# Revit family: Grohe_PlumbingFixture_TempestaCosmopolitan100_ShowerRailSet_27579002a
name_source: partatom
category: Plumbing Fixtures
revit_build: Autodesk Revit 2018 (Build: 20190510_1515(x64)
units: mm (PartAtom-declared; Revit-internal decimal feet)

## family parameters
Cut with Voids When Loaded = No
Host = Face
OmniClass Number = 23.65.00.00
OmniClass Title = Supply and Distribution of Liquids and Gases
Part Type = Normal
Room Calculation Point = No
Round Connector Dimension = Use Diameter
Shared = No

## types (1)
- 27579002
    ADACompliant = No
    Assembly Code = D2010700
    BIMObjectName = Grohe_PlumbingFixture_TempestaCosmopolitan100_ShowerRailSet_27579002
    ClassificationName = Uniclass 2015
    ClassificationValue = Pr_40_20_87_75
    ColdWaterConnectionDiameter = 10 mm  [stored 0.0328084 ft]
    Color = Chrome
    Default Elevation = 0 mm  [stored 0 ft]
    Description = Add affordable luxury to your bathroom and change the way you shower with the GROHE New Tempesta Cosmopolitan 100 shower rail set. The stylish kit contains a hand shower with a white 100mm spray plate, a 600mm shower rail and a 1750mm hose. It’s packed with a lot of smart features. GROHE EcoJoy technology limits water flow to 9.5 l/m, which saves water and money without compromising performance. The hand shower comes with three spray options so you can tailor it to your mood: the light-as-air GROHE Rain O² Spray with added oxygen for a softer feel, the gentle summer shower feel of Rain Spray and the invigorating Massage Spray. GROHE DreamSpray ensures that whichever spray pattern you select, the flow from each and every nozzle will be just right, making your shower as comfortable and enjoyable as can be. Its SpeedClean silicone nozzles are designed to brush free of limescale with a simple wipe, and the durable GROHE StarLight chrome finish keeps the whole set looking pristine. And an Inner WaterGuide prevents the surface of the hand shower from getting too hot, in order to protect both your sensitive skin and the lustrous chrome finish.
    DocumentationCertificates = https://www.bimstore.co
    DocumentationInstallationGuide = https://www.bimstore.co
    DocumentationLiterature = https://www.bimstore.co
    DocumentationMaintenance = https://www.bimstore.co
    DocumentationTechnical = https://www.bimstore.co
    DurationUnit = Years
    Ecojoy = No
    ExpectedLife = 0
    Features = Add affordable luxury to your bathroom and change the way you shower with the GROHE New Tempesta Cosmopolitan 100 shower rail set. The stylish kit contains a hand shower with a white 100mm spray plate, a 600mm shower rail and a 1750mm hose. It’s packed with a lot of smart features. GROHE EcoJoy technology limits water flow to 9.5 l/m, which saves water and money without compromising performance. The hand shower comes with three spray options so you can tailor it to your mood: the light-as-air GROHE Rain O² Spray with added oxygen for a softer feel, the gentle summer shower feel of Rain Spray and the invigorating Massage Spray. GROHE DreamSpray ensures that whichever spray pattern you select, the flow from each and every nozzle will be just right, making your shower as comfortable and enjoyable as can be. Its SpeedClean silicone nozzles are designed to brush free of limescale with a simple wipe, and the durable GROHE StarLight chrome finish keeps the whole set looking pristine. And an Inner WaterGuide prevents the surface of the hand shower from getting too hot, in order to protect both your sensitive skin and the lustrous chrome finish.
    HotWaterConnectionDiameter = 10 mm  [stored 0.0328084 ft]
    IfcExportAs = IfcPipeFitting
    IfcExportType = IfcPipeFittingType
    Keynote = N13
    LowEmittingMaterial = No
    Manufacturer = Grohe
    ManufacturerName = Grohe
    MasterformatNumber = 01 52 19
    MasterformatTitle = Sanitary Facilities
    Model = Tempesta Cosmopolitan 100 - Shower rail set 3 sprays
    ModelNumber = 27579002
    ModelReference = Tempesta Cosmopolitan 100 - Shower rail set 3 sprays
    NBSDescription = Shower fittings package
    NBSObjectName = Grohe - Shower fittings package
    NBSReference = 45-35-70/330
    NominalDepth = 0 mm  [stored 0 ft]
    NominalHeight = 0 mm  [stored 0 ft]
    NominalLength = 0 mm  [stored 0 ft]
    PrimaryMaterial = Steel, Chrome Plated
    ProductDocumentationLink = https://www.grohe.co.uk
    ProductPageURL = https://www.grohe.co.uk
    ProductionYear = 2020
    Type Comments = 27579002
    TypeName = Tempesta Cosmopolitan 100 - Shower rail set 3 sprays
    URL = https://www.grohe.co.uk
    WarrantyDurationLabor = 0
    WarrantyDurationParts = 0
    WarrantyDurationUnit = Years
    _BSBibleVersion = 16
    _BimSpecGuid = 0
    _CurrentRevision = 1
    _DistributedBy = www.bimstore.co
    _ObjectUserGuide = https://www.bimstore.co

note: [stored X ft] marks values corroborated as IEEE doubles in the binary element streams (Revit-internal decimal feet)

## geometry (parser evidence)
native form markers: Sweep x2
no freeform markers — native parametric forms only
